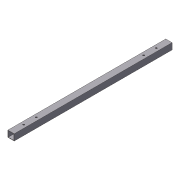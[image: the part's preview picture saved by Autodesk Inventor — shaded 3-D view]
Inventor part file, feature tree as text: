
AUTODESK INVENTOR PART (.ipt)
format: ipt  version: 2012 (Build 160160000, 160)  size: 97,792 bytes
history: native  units: in
note: dims shown in document units (in); Inventor stores cm internally (conversion verified against a paired STEP export)
features: extrude x2, sketch x2, shell x1
ambient origin geometry x8: Origin, YZ Plane, XZ Plane, XY Plane, X Axis, Y Axis, Z Axis, Center Point
bodies: Solid1 (feature_tree)
feature tree (5):
  extrude  "Extrusion1"  Depth=1.0in
  shell  "Shell1"  Thickness=25.0in
  extrude  "Extrusion2"  Depth=2.0in
  sketch  "Sketch1"  dims[d0=1.0in d1=1.0in d2=25.0in d3=0.0in]
  sketch  "Sketch2"  dims[d4=0.0625in d7=2.0in d8=2.0in d9=0.5in d10=0.5in d11=0.25in d12=0.25in d13=0.5in d14=0.5in d15=2.0in d16=2.0in d17=0.25in d18=0.25in d19=35.0in d20=0.0in]
